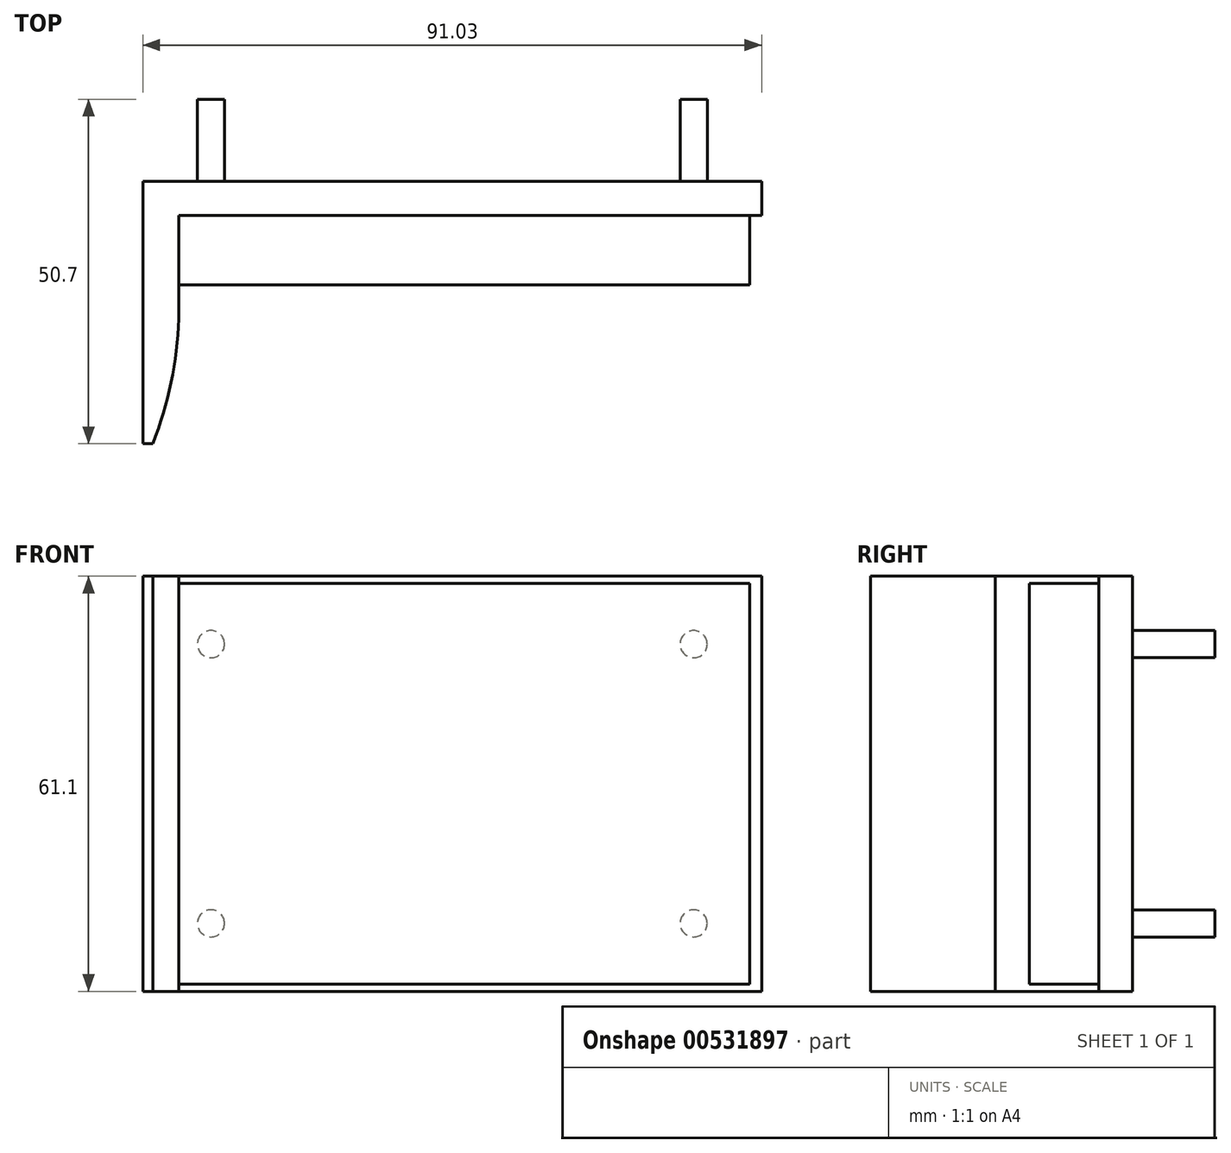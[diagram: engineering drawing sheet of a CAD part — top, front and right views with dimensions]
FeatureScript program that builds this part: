
annotation { "Feature Type Name" : "Feature", "Feature Type Description" : "" }
export const myFeature = defineFeature(function(context is Context, id is Id, definition is map)
    precondition{}
    {
        {
            var Q0;
            Q0=qCreatedBy(makeId("Front.planeOp"),FACE);
            var sketch = newSketch(context, id + "F0", { "sketchPlane" : qUnion([Q0])});
            skLineSegment(sketch, "E0.bottom", {"start": v(42, 29.5) * mm, "end": v(-42, 29.5) * mm});
            skLineSegment(sketch, "E0.top", {"start": v(42, -29.5) * mm, "end": v(-42, -29.5) * mm});
            skLineSegment(sketch, "E0.left", {"start": v(42, 29.5) * mm, "end": v(42, -29.5) * mm});
            skLineSegment(sketch, "E0.right", {"start": v(-42, 29.5) * mm, "end": v(-42, -29.5) * mm});
            skPoint(sketch, "E0.middle", {"position": v(0, 0) * mm});
            skSolve(sketch);
        }
        {
            var Q0;
            Q0 = qSketchRegion(id + "F0", true);
            extrude(context, id + "F1", {"entities" : qUnion([Q0]), "depth" : 10.2 * mm, "offsetDistance" : 25 * mm});
        }
        {
            var Q0;
            Q0=makeQuery(id+"F1.opExtrude","CAP_FACE",FACE,{"disambiguationData":[OSD([sQuery(id+"F0.wireOp",EDGE,"E0.bottom"),sQuery(id+"F0.wireOp",EDGE,"E0.top"),sQuery(id+"F0.wireOp",EDGE,"E0.left"),sQuery(id+"F0.wireOp",EDGE,"E0.right")])],"isStart":true});
            var sketch = newSketch(context, id + "F2", { "sketchPlane" : qUnion([Q0])});
            skLineSegment(sketch, "E1.bottom", {"start": v(43.75, 30.55) * mm, "end": v(-43.75, 30.55) * mm});
            skLineSegment(sketch, "E1.top", {"start": v(43.75, -30.55) * mm, "end": v(-43.75, -30.55) * mm});
            skLineSegment(sketch, "E1.left", {"start": v(43.75, 30.55) * mm, "end": v(43.75, -30.55) * mm});
            skLineSegment(sketch, "E1.right", {"start": v(-43.75, 30.55) * mm, "end": v(-43.75, -30.55) * mm});
            skPoint(sketch, "E1.middle", {"position": v(0, 0) * mm});
            skLineSegment(sketch, "E2.bottom", {"start": v(43.75, 30.55) * mm, "end": v(47.28, 30.55) * mm});
            skLineSegment(sketch, "E2.top", {"start": v(43.75, -30.55) * mm, "end": v(47.28, -30.55) * mm});
            skLineSegment(sketch, "E2.right", {"start": v(47.28, 30.55) * mm, "end": v(47.28, -30.55) * mm});
            skSolve(sketch);
        }
        {
            var Q0;
            Q0 = qSketchRegion(id + "F2", true);
            extrude(context, id + "F3", {"entities" : qUnion([Q0]), "operationType" : NewBodyOperationType.ADD, "depth" : 5 * mm, "offsetDistance" : 25 * mm});
        }
        {
            var Q0;
            Q0=makeQuery(id+"F3.opExtrude","CAP_FACE",FACE,{"disambiguationData":[OSD([sQuery(id+"F2.wireOp",EDGE,"E1.bottom"),sQuery(id+"F2.wireOp",EDGE,"E1.top"),sQuery(id+"F2.wireOp",EDGE,"E1.right"),sQuery(id+"F2.wireOp",EDGE,"E2.bottom"),sQuery(id+"F2.wireOp",EDGE,"E2.top"),sQuery(id+"F2.wireOp",EDGE,"E2.right")])],"isStart":true});
            var sketch = newSketch(context, id + "F4", { "sketchPlane" : qUnion([Q0])});
            skLineSegment(sketch, "E3.bottom", {"start": v(-47.28, 30.55) * mm, "end": v(-42, 30.55) * mm});
            skLineSegment(sketch, "E3.top", {"start": v(-47.28, -30.55) * mm, "end": v(-42, -30.55) * mm});
            skLineSegment(sketch, "E3.left", {"start": v(-47.28, 30.55) * mm, "end": v(-47.28, -30.55) * mm});
            skLineSegment(sketch, "E3.right", {"start": v(-42, 30.55) * mm, "end": v(-42, -30.55) * mm});
            skSolve(sketch);
        }
        {
            var Q0;
            Q0 = qSketchRegion(id + "F4", true);
            extrude(context, id + "F5", {"entities" : qUnion([Q0]), "operationType" : NewBodyOperationType.ADD, "depth" : 33.6 * mm, "offsetDistance" : 25 * mm});
        }
        {
            var Q0;
            Q0=makeQuery(id+"F5.boolean.opBoolean","MERGE",FACE,{"derivedFrom":[makeQuery(id+"F3.opExtrude","SWEPT_FACE",FACE,{"disambiguationData":[OSD([sQuery(id+"F2.wireOp",EDGE,"E1.top"),sQuery(id+"F2.wireOp",EDGE,"E2.top")])]}),makeQuery(id+"F5.opExtrude","SWEPT_FACE",FACE,{"disambiguationData":[OSD([sQuery(id+"F4.wireOp",EDGE,"E3.top")])]})]});
            var sketch = newSketch(context, id + "F6", { "sketchPlane" : qUnion([Q0])});
            skArc(sketch, "E4", {"start": v(-42, 15.22) * mm, "mid": v(-43.15, 24.57) * mm, "end": v(-45.83, 33.6) * mm});
            skLineSegment(sketch, "E5", {"start": v(-45.83, 33.6) * mm, "end": v(-42, 33.6) * mm});
            skLineSegment(sketch, "E6", {"start": v(-42, 33.6) * mm, "end": v(-42, 15.22) * mm});
            skSolve(sketch);
        }
        {
            var Q0;
            Q0 = qSketchRegion(id + "F6", true);
            extrude(context, id + "F7", {"entities" : qUnion([Q0]), "operationType" : NewBodyOperationType.REMOVE, "oppositeDirection" : true, "depth" : 69.2 * mm, "offsetDistance" : 25 * mm});
        }
        {
            var Q0;
            Q0=makeQuery(id+"F3.opExtrude","CAP_FACE",FACE,{"disambiguationData":[OSD([sQuery(id+"F2.wireOp",EDGE,"E1.bottom"),sQuery(id+"F2.wireOp",EDGE,"E1.top"),sQuery(id+"F2.wireOp",EDGE,"E1.right"),sQuery(id+"F2.wireOp",EDGE,"E2.bottom"),sQuery(id+"F2.wireOp",EDGE,"E2.top"),sQuery(id+"F2.wireOp",EDGE,"E2.right")])],"isStart":false});
            var sketch = newSketch(context, id + "F8", { "sketchPlane" : qUnion([Q0])});
            skCircle(sketch, "E7", {"center": v(-33.75, 20.55) * mm, "radius": 2 * mm});
            skCircle(sketch, "E8", {"center": v(37.28, 20.55) * mm, "radius": 2 * mm});
            skCircle(sketch, "E9", {"center": v(37.28, -20.55) * mm, "radius": 2 * mm});
            skCircle(sketch, "E10", {"center": v(-33.75, -20.55) * mm, "radius": 2 * mm});
            skSolve(sketch);
        }
        {
            var Q0;
            Q0 = qSketchRegion(id + "F8", true);
            extrude(context, id + "F9", {"entities" : qUnion([Q0]), "operationType" : NewBodyOperationType.ADD, "depth" : 12.1 * mm, "offsetDistance" : 25 * mm});
        }
    });
